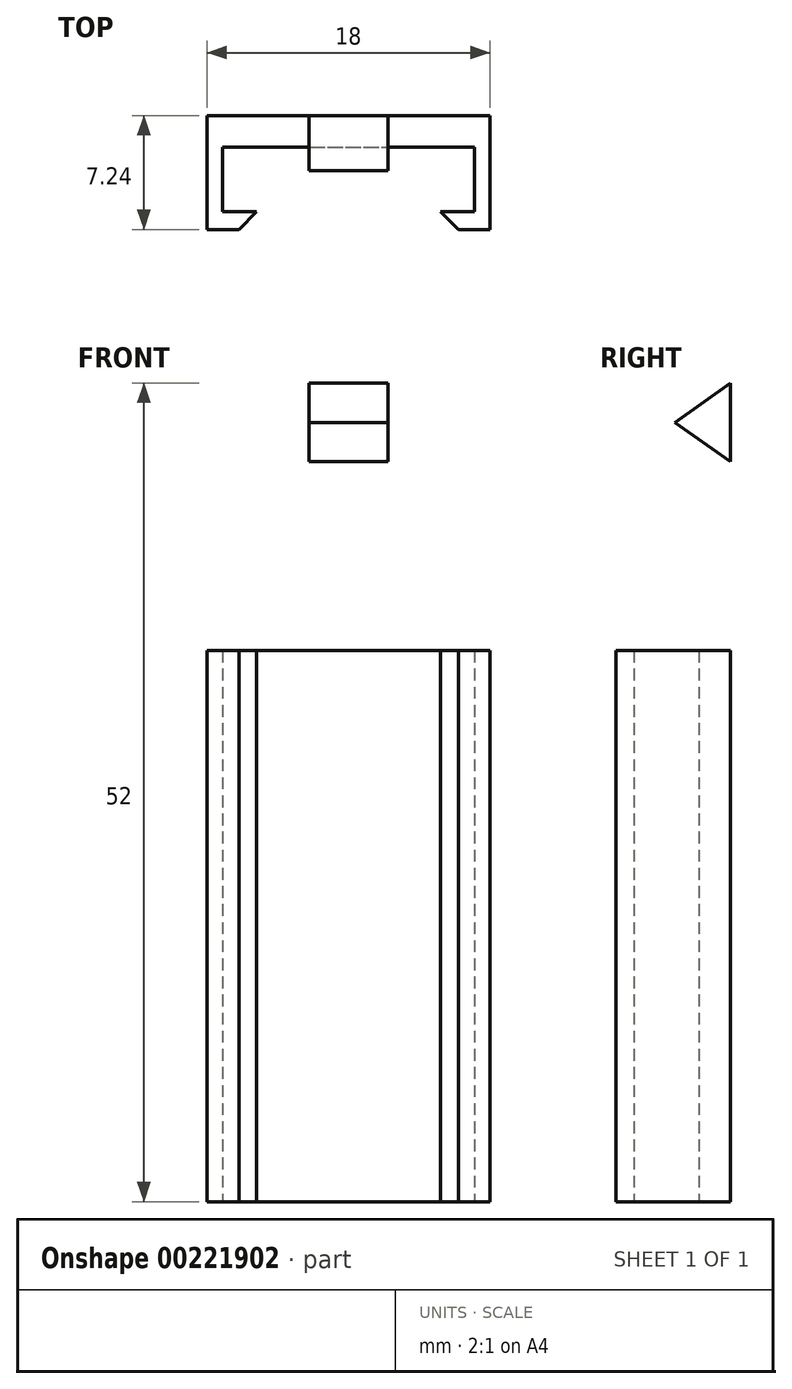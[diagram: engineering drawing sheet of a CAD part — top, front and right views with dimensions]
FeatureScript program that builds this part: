
annotation { "Feature Type Name" : "Feature", "Feature Type Description" : "" }
export const myFeature = defineFeature(function(context is Context, id is Id, definition is map)
    precondition{}
    {
        {
            var Q0;
            Q0=qCreatedBy(makeId("Top.planeOp"),FACE);
            var sketch = newSketch(context, id + "F0", { "sketchPlane" : qUnion([Q0])});
            skLineSegment(sketch, "E0.left", {"start": v(-9, 7.24) * mm, "end": v(-9, 0) * mm});
            skLineSegment(sketch, "E1", {"start": v(-9, 7.24) * mm, "end": v(0, 7.24) * mm});
            skLineSegment(sketch, "E2", {"start": v(-9, 0) * mm, "end": v(-6.97, 0) * mm});
            skLineSegment(sketch, "E3", {"start": v(-6.97, 0) * mm, "end": v(-5.83, 1.14) * mm});
            skLineSegment(sketch, "E4", {"start": v(-5.83, 1.14) * mm, "end": v(-8, 1.14) * mm});
            skLineSegment(sketch, "E5", {"start": v(-8, 1.14) * mm, "end": v(-8, 5.24) * mm});
            skLineSegment(sketch, "E6", {"start": v(-8, 5.24) * mm, "end": v(-0.18, 5.24) * mm});
            skLineSegment(sketch, "E7", {"start": v(-0.18, 5.24) * mm, "end": v(0, 5.24) * mm});
            skLineSegment(sketch, "E8.MirrorCS", {"start": v(9, 7.24) * mm, "end": v(0, 7.24) * mm});
            skLineSegment(sketch, "E9.MirrorCS", {"start": v(8, 5.24) * mm, "end": v(0.18, 5.24) * mm});
            skLineSegment(sketch, "E10.MirrorCS", {"start": v(9, 7.24) * mm, "end": v(9, 0) * mm});
            skLineSegment(sketch, "E11.MirrorCS", {"start": v(8, 1.14) * mm, "end": v(8, 5.24) * mm});
            skLineSegment(sketch, "E12.MirrorCS", {"start": v(5.83, 1.14) * mm, "end": v(8, 1.14) * mm});
            skLineSegment(sketch, "E13.MirrorCS", {"start": v(6.97, 0) * mm, "end": v(5.83, 1.14) * mm});
            skLineSegment(sketch, "E14.MirrorCS", {"start": v(9, 0) * mm, "end": v(6.97, 0) * mm});
            skLineSegment(sketch, "E15", {"start": v(0, 5.24) * mm, "end": v(0.18, 5.24) * mm});
            skSolve(sketch);
        }
        {
            var Q0;
            Q0 = qSketchRegion(id + "F0", true);
            extrude(context, id + "F1", {"entities" : qUnion([Q0]), "depth" : 35 * mm});
        }
        {
            var Q0;
            Q0=qCreatedBy(makeId("Right.planeOp"),FACE);
            var sketch = newSketch(context, id + "F2", { "sketchPlane" : qUnion([Q0])});
            skLineSegment(sketch, "E16", {"start": v(7.24, 24.99) * mm, "end": v(7.24, 53.34) * mm, "construction": true});
            skLineSegment(sketch, "E17", {"start": v(7.24, 47) * mm, "end": v(3.74, 49.5) * mm});
            skLineSegment(sketch, "E18", {"start": v(3.74, 49.5) * mm, "end": v(7.24, 52) * mm});
            skLineSegment(sketch, "E19", {"start": v(7.24, 47) * mm, "end": v(7.24, 52) * mm});
            skSolve(sketch);
        }
        {
            var Q0;
            Q0 = qSketchRegion(id + "F2", true);
            extrude(context, id + "F3", {"entities" : qUnion([Q0]), "depth" : 2.5 * mm, "hasSecondDirection" : true, "secondDirectionOppositeDirection" : true, "secondDirectionDepth" : 2.5 * mm});
        }
    });
